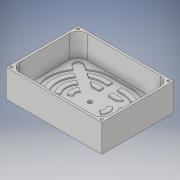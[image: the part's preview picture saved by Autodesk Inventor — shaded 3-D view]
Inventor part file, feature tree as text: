
AUTODESK INVENTOR PART (.ipt)
format: ipt  version: 2018 (Build 220112000, 112)  size: 313,344 bytes
history: native  units: in
note: dims shown in document units (in); Inventor stores cm internally (conversion verified against a paired STEP export)
features: extrude x6, sketch x5, projected_geometry x5, hole x2, fillet x1
ambient origin geometry x8: Origin, YZ Plane, XZ Plane, XY Plane, X Axis, Y Axis, Z Axis, Center Point
bodies: Solid1 (feature_tree)
feature tree (19):
  sketch  "Sketch1"  dims[d0=9.125in d1=0.5in]
  extrude  "Extrusion1"  Depth=0.5in
  extrude  "Extrusion2"  Depth=6.5in
  fillet  "Fillet1"  Radius=0.25in
  sketch  "Sketch2"  dims[d2=0.5in d3=6.5in d4=0.25in]
  extrude  "Extrusion3"  Depth=0.5in TaperAngle=0.0deg
  extrude  "Extrusion4"  Depth=3.5in
  extrude  "Extrusion5"  Depth=0.5in
  extrude  "Extrusion6"  Depth=0.5in
  hole  "Hole2"  [1 undecoded]
  sketch  "Sketch3"  dims[d5=2.5591in d6=0.0in d7=0.5in d8=0.0in]
  projected_geometry  "Projected Loop1"
  sketch  "Sketch4"  dims[d9=1.0in d10=3.5in]
  projected_geometry  "Projected Loop2"
  projected_geometry  "Projected Loop3"
  projected_geometry  "Projected Loop4"
  projected_geometry  "Projected Loop5"
  sketch  "Sketch5"  dims[d11=2.25in d12=0.5in d13=0.5in d14=0.5in d15=0.5in d17=0.5in d18=0.5in d19=0.45in d20=1.0in d21=0.0in d22=0.125in d23=0.0in d24=1.0in d25=1.0in d26=1.0in d27=0.125in d28=0.0in d29=0.125in d30=0.0in d31=0.266in d32=0.75in d33=0.375in d34=0.25in d35=0.5635in d36=1.0in d37=0.0in]
  hole  "Hole1"  [1 undecoded]
note: 2 required parameter values undecoded (feature->parameter linkage not recoverable at this tier; creation-order binding heuristic only, values carry confidence <= 0.55)
